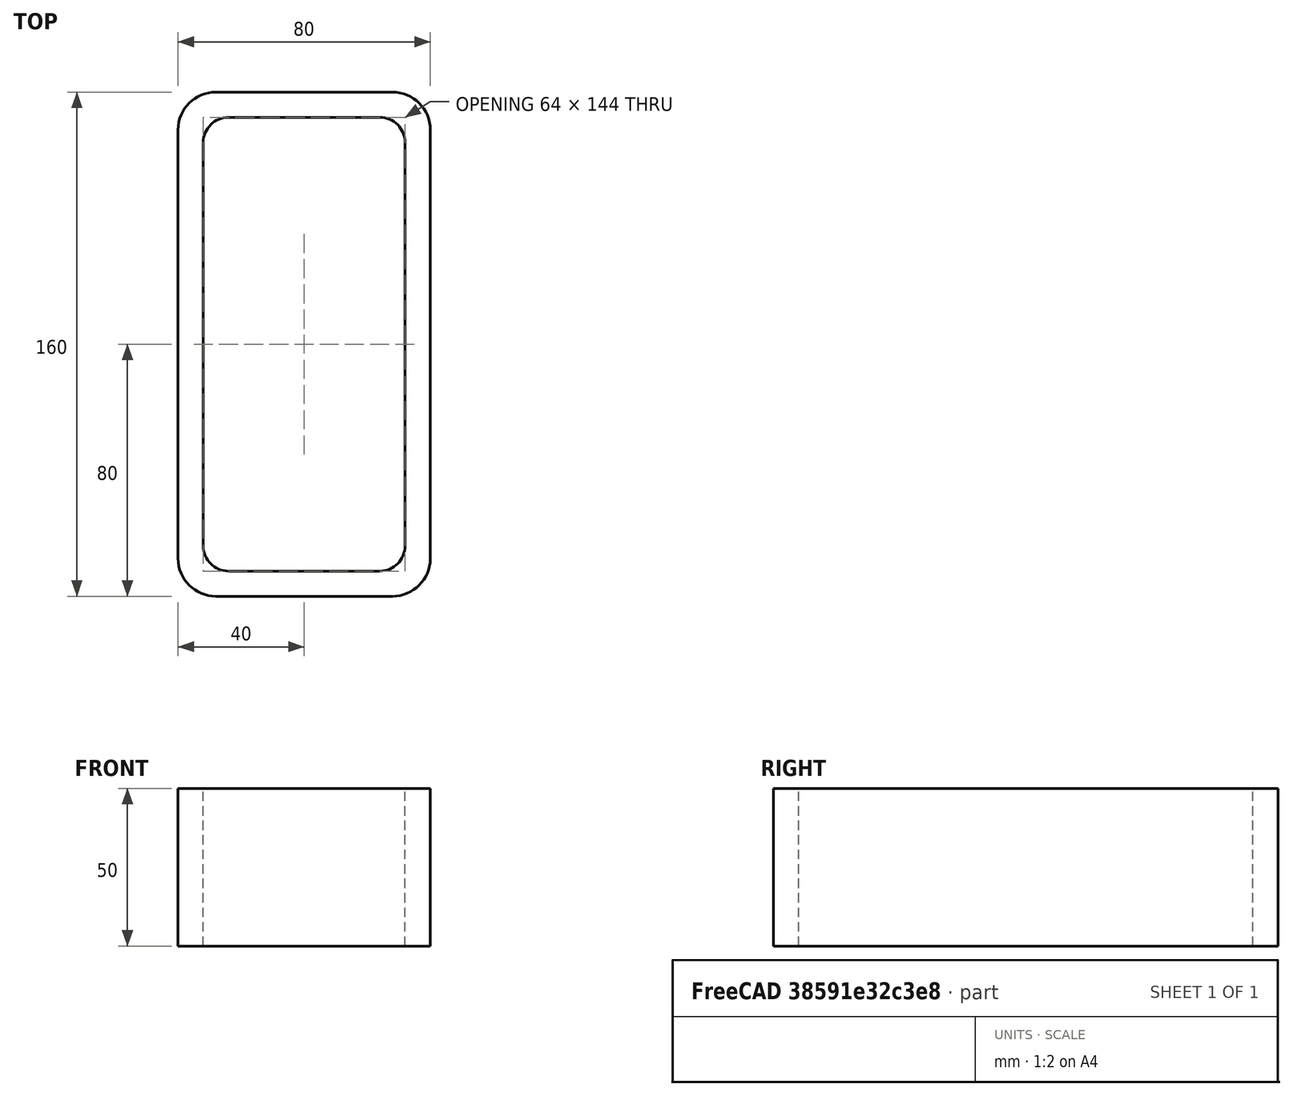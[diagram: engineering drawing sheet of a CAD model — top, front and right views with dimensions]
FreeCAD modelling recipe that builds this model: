
FCSTD DOCUMENT  (FreeCAD 0.15R4671 (Git))
Label: Rectangular hollow section 160x80x8 EN10219 S235JRH
License: All rights reserved
LicenseURL: http://en.wikipedia.org/wiki/All_rights_reserved
objects: Sketcher::SketchObject×1, Part::Extrusion×1
note: 2 computed .brp shape members not serialized (recipe doc carries the construction recipe); baked Part::Feature solids carry a one-line shape summary decoded from their .brp

FEATURE [Sketcher::SketchObject] Sketch
  sketch-geometry (16):
    g0: LineSegment StartX=-24 StartY=72 StartZ=0 EndX=24 EndY=72 EndZ=0
    g1: LineSegment StartX=32 StartY=64 StartZ=0 EndX=32 EndY=-64 EndZ=0
    g2: LineSegment StartX=24 StartY=-72 StartZ=0 EndX=-24 EndY=-72 EndZ=0
    g3: LineSegment StartX=-32 StartY=-64 StartZ=0 EndX=-32 EndY=64 EndZ=0
    g4: LineSegment StartX=-28 StartY=80 StartZ=0 EndX=28 EndY=80 EndZ=0
    g5: LineSegment StartX=40 StartY=68 StartZ=0 EndX=40 EndY=-68 EndZ=0
    g6: LineSegment StartX=28 StartY=-80 StartZ=0 EndX=-28 EndY=-80 EndZ=0
    g7: LineSegment StartX=-40 StartY=-68 StartZ=0 EndX=-40 EndY=68 EndZ=0
    g8: ArcOfCircle CenterX=-24 CenterY=64 CenterZ=0 NormalX=0 NormalY=0 NormalZ=1 Radius=8 StartAngle=1.5708 EndAngle=3.14159
    g9: ArcOfCircle CenterX=24 CenterY=64 CenterZ=0 NormalX=0 NormalY=0 NormalZ=1 Radius=8 StartAngle=0 EndAngle=1.5708
    g10: ArcOfCircle CenterX=24 CenterY=-64 CenterZ=0 NormalX=0 NormalY=0 NormalZ=1 Radius=8 StartAngle=4.71239 EndAngle=6.28319
    g11: ArcOfCircle CenterX=-24 CenterY=-64 CenterZ=0 NormalX=0 NormalY=0 NormalZ=1 Radius=8 StartAngle=3.14159 EndAngle=4.71239
    g12: ArcOfCircle CenterX=28 CenterY=68 CenterZ=0 NormalX=0 NormalY=0 NormalZ=1 Radius=12 StartAngle=0 EndAngle=1.5708
    g13: ArcOfCircle CenterX=28 CenterY=-68 CenterZ=0 NormalX=0 NormalY=0 NormalZ=1 Radius=12 StartAngle=4.71239 EndAngle=6.28319
    g14: ArcOfCircle CenterX=-28 CenterY=-68 CenterZ=0 NormalX=0 NormalY=0 NormalZ=1 Radius=12 StartAngle=3.14159 EndAngle=4.71239
    g15: ArcOfCircle CenterX=-28 CenterY=68 CenterZ=0 NormalX=0 NormalY=0 NormalZ=1 Radius=12 StartAngle=1.5708 EndAngle=3.14159
  constraints (36):
    c: Horizontal(g2)
    c: Vertical(g3)
    c: Horizontal(g6)
    c: Vertical(g7)
    c: Tangent(g3,g8) = 1.5708
    c: Tangent(g0,g8) = 1.5708
    c: Tangent(g0,g9) = 1.5708
    c: Tangent(g1,g9) = 1.5708
    c: Tangent(g1,g10) = 1.5708
    c: Tangent(g2,g10) = 1.5708
    c: Tangent(g2,g11) = 1.5708
    c: Tangent(g3,g11) = 1.5708
    c: Tangent(g4,g12) = 1.5708
    c: Tangent(g5,g12) = 1.5708
    c: Tangent(g5,g13) = 1.5708
    c: Tangent(g6,g13) = 1.5708
    c: Tangent(g6,g14) = 1.5708
    c: Tangent(g7,g14) = 1.5708
    c: Tangent(g7,g15) = 1.5708
    c: Tangent(g4,g15) = 1.5708
    c: Equal(g9,g8)
    c: Equal(g9,g11)
    c: Equal(g9,g10)
    c: Equal(g12,g15)
    c: Equal(g12,g14)
    c: Equal(g12,g13)
    c: Symmetric(g4,g6,g-1)
    c: Symmetric(g7,g5,g-2)
    c: DistanceY(g4,g6) = -160
    c: DistanceX(g7,g5) = 80
    c: Symmetric(g3,g1,g-2)
    c: Symmetric(g0,g2,g-1)
    c: DistanceY(g0,g4) = 8
    c: DistanceX(g5,g1) = -8
    c: Radius(g9) = 8
    c: Radius(g12) = 12
FEATURE [Part::Extrusion] Extrude  label="Rectangular hollow section 160x80x8 EN10219 S235JRH"
  Base = -> Sketch
  Dir = (0,0,50)
  Solid = true
